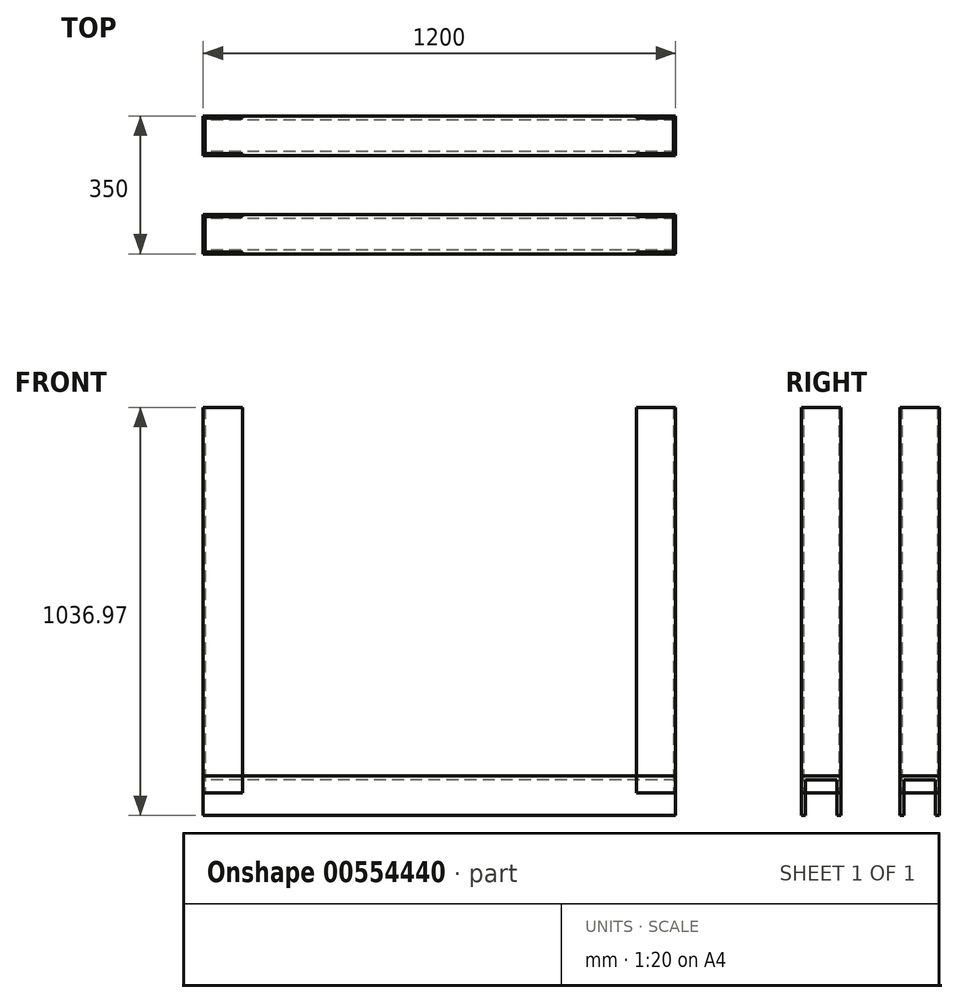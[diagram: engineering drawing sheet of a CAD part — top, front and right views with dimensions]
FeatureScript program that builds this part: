
annotation { "Feature Type Name" : "Feature", "Feature Type Description" : "" }
export const myFeature = defineFeature(function(context is Context, id is Id, definition is map)
    precondition{}
    {
        {
            var Q0;
            Q0=qCreatedBy(makeId("Right.planeOp"),FACE);
            var sketch = newSketch(context, id + "F0", { "sketchPlane" : qUnion([Q0])});
            skLineSegment(sketch, "E0", {"start": v(251.35, -56.97) * mm, "end": v(-262.16, -56.97) * mm, "construction": true});
            skLineSegment(sketch, "E1.top", {"start": v(-175, 43.03) * mm, "end": v(-75, 43.03) * mm});
            skLineSegment(sketch, "E1.left", {"start": v(-175, -56.97) * mm, "end": v(-175, 43.03) * mm});
            skLineSegment(sketch, "E1.right", {"start": v(-75, -56.97) * mm, "end": v(-75, 43.03) * mm});
            skLineSegment(sketch, "E2.top", {"start": v(75, 43.03) * mm, "end": v(175, 43.03) * mm});
            skLineSegment(sketch, "E2.left", {"start": v(75, -56.97) * mm, "end": v(75, 43.03) * mm});
            skLineSegment(sketch, "E2.right", {"start": v(175, -56.97) * mm, "end": v(175, 43.03) * mm});
            skLineSegment(sketch, "E3", {"start": v(-175, -56.97) * mm, "end": v(-165, -56.97) * mm});
            skLineSegment(sketch, "E4", {"start": v(-165, -56.97) * mm, "end": v(-165, 33.03) * mm});
            skLineSegment(sketch, "E5", {"start": v(-165, 33.03) * mm, "end": v(-85, 33.03) * mm});
            skLineSegment(sketch, "E6", {"start": v(-85, 33.03) * mm, "end": v(-85, -56.97) * mm});
            skLineSegment(sketch, "E7", {"start": v(-85, -56.97) * mm, "end": v(-75, -56.97) * mm});
            skLineSegment(sketch, "E8", {"start": v(75, -56.97) * mm, "end": v(85, -56.97) * mm});
            skLineSegment(sketch, "E9", {"start": v(85, -56.97) * mm, "end": v(85, 33.03) * mm});
            skLineSegment(sketch, "E10", {"start": v(85, 33.03) * mm, "end": v(165, 33.03) * mm});
            skLineSegment(sketch, "E11", {"start": v(165, 33.03) * mm, "end": v(165, -56.97) * mm});
            skLineSegment(sketch, "E12", {"start": v(165, -56.97) * mm, "end": v(175, -56.97) * mm});
            skSolve(sketch);
        }
        {
            var Q0;
            Q0=makeQuery(id+"F0.imprint","IMPRINT",FACE,{"disambiguationData":[TD([[makeQuery(id+"F0.imprint","IMPRINT",EDGE,{"derivedFrom":sQuery(id+"F0.wireOp",EDGE,"E1.top")}),-1.0]])]});
            var Q1;
            Q1=makeQuery(id+"F0.imprint","IMPRINT",FACE,{"disambiguationData":[TD([[makeQuery(id+"F0.imprint","IMPRINT",EDGE,{"derivedFrom":sQuery(id+"F0.wireOp",EDGE,"E2.top")}),-1.0]])]});
            extrude(context, id + "F1", {"entities" : qUnion([Q0, Q1]), "endBound" : BoundingType.SYMMETRIC, "depth" : 1200 * mm, "offsetDistance" : 25 * mm});
        }
        {
            var Q0;
            Q0=qCreatedBy(makeId("Top.planeOp"),FACE);
            var sketch = newSketch(context, id + "F2", { "sketchPlane" : qUnion([Q0])});
            skLineSegment(sketch, "E13", {"start": v(-595, 170) * mm, "end": v(-595, 80) * mm});
            skLineSegment(sketch, "E14", {"start": v(-595, 80) * mm, "end": v(-500, 80) * mm});
            skLineSegment(sketch, "E15", {"start": v(-500, 75) * mm, "end": v(-500, 80) * mm});
            skLineSegment(sketch, "E16", {"start": v(-500, 75) * mm, "end": v(-600, 75) * mm});
            skLineSegment(sketch, "E17", {"start": v(-600, 75) * mm, "end": v(-600, 175) * mm});
            skLineSegment(sketch, "E18", {"start": v(-600, 175) * mm, "end": v(-500, 175) * mm});
            skLineSegment(sketch, "E19", {"start": v(-500, 170) * mm, "end": v(-500, 175) * mm});
            skLineSegment(sketch, "E20", {"start": v(-500, 170) * mm, "end": v(-595, 170) * mm});
            skLineSegment(sketch, "E21", {"start": v(-595, -80) * mm, "end": v(-595, -170) * mm});
            skLineSegment(sketch, "E22", {"start": v(-595, -170) * mm, "end": v(-500, -170) * mm});
            skLineSegment(sketch, "E23", {"start": v(-500, -175) * mm, "end": v(-500, -170) * mm});
            skLineSegment(sketch, "E24", {"start": v(-500, -175) * mm, "end": v(-600, -175) * mm});
            skLineSegment(sketch, "E25", {"start": v(-600, -175) * mm, "end": v(-600, -75) * mm});
            skLineSegment(sketch, "E26", {"start": v(-600, -75) * mm, "end": v(-500, -75) * mm});
            skLineSegment(sketch, "E27", {"start": v(-500, -80) * mm, "end": v(-500, -75) * mm});
            skLineSegment(sketch, "E28", {"start": v(-500, -80) * mm, "end": v(-595, -80) * mm});
            skLineSegment(sketch, "E29", {"start": v(600, 175) * mm, "end": v(600, 75) * mm});
            skLineSegment(sketch, "E30", {"start": v(600, 75) * mm, "end": v(500, 75) * mm});
            skLineSegment(sketch, "E31", {"start": v(500, 75) * mm, "end": v(500, 80) * mm});
            skLineSegment(sketch, "E32", {"start": v(500, 80) * mm, "end": v(595, 80) * mm});
            skLineSegment(sketch, "E33", {"start": v(595, 80) * mm, "end": v(595, 170) * mm});
            skLineSegment(sketch, "E34", {"start": v(595, 170) * mm, "end": v(500, 170) * mm});
            skLineSegment(sketch, "E35", {"start": v(500, 170) * mm, "end": v(500, 175) * mm});
            skLineSegment(sketch, "E36", {"start": v(500, 175) * mm, "end": v(600, 175) * mm});
            skLineSegment(sketch, "E37", {"start": v(600, -75) * mm, "end": v(500, -75) * mm});
            skLineSegment(sketch, "E38", {"start": v(500, -75) * mm, "end": v(500, -80) * mm});
            skLineSegment(sketch, "E39", {"start": v(500, -80) * mm, "end": v(595, -80) * mm});
            skLineSegment(sketch, "E40", {"start": v(595, -80) * mm, "end": v(595, -170) * mm});
            skLineSegment(sketch, "E41", {"start": v(595, -170) * mm, "end": v(500, -170) * mm});
            skLineSegment(sketch, "E42", {"start": v(500, -170) * mm, "end": v(500, -175) * mm});
            skLineSegment(sketch, "E43", {"start": v(500, -175) * mm, "end": v(600, -175) * mm});
            skLineSegment(sketch, "E44", {"start": v(600, -75) * mm, "end": v(600, -175) * mm});
            skSolve(sketch);
        }
        {
            var Q0;
            Q0 = qSketchRegion(id + "F2", true);
            extrude(context, id + "F3", {"entities" : qUnion([Q0]), "depth" : 980 * mm, "offsetDistance" : 25 * mm});
        }
    });
